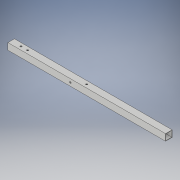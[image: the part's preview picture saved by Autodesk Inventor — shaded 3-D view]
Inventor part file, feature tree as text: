
AUTODESK INVENTOR PART (.ipt)
format: ipt  version: 2017 (Build 210142000, 142)  size: 121,856 bytes
history: native  units: in
note: dims shown in document units (in); Inventor stores cm internally (conversion verified against a paired STEP export)
features: extrude x3, sketch x3
ambient origin geometry x8: Origin, YZ Plane, XZ Plane, XY Plane, X Axis, Y Axis, Z Axis, Center Point
bodies: Solid1 (feature_tree)
feature tree (6):
  extrude  "Extrusion1"  Depth=1.0in
  extrude  "Extrusion2"  Depth=24.0in TaperAngle=0.0deg
  extrude  "Extrusion3"  Depth=1.0in
  sketch  "Sketch1"  dims[d0=1.0in d1=1.0in]
  sketch  "Sketch2"  dims[d2=0.0625in d3=24.0in d4=0.0in]
  sketch  "Sketch3"  dims[d5=0.25in d6=1.5in d7=2.5in d8=11.5in d9=1.0in d10=0.0in d11=0.25in d12=9.5in d13=1.0in d14=0.0in]
